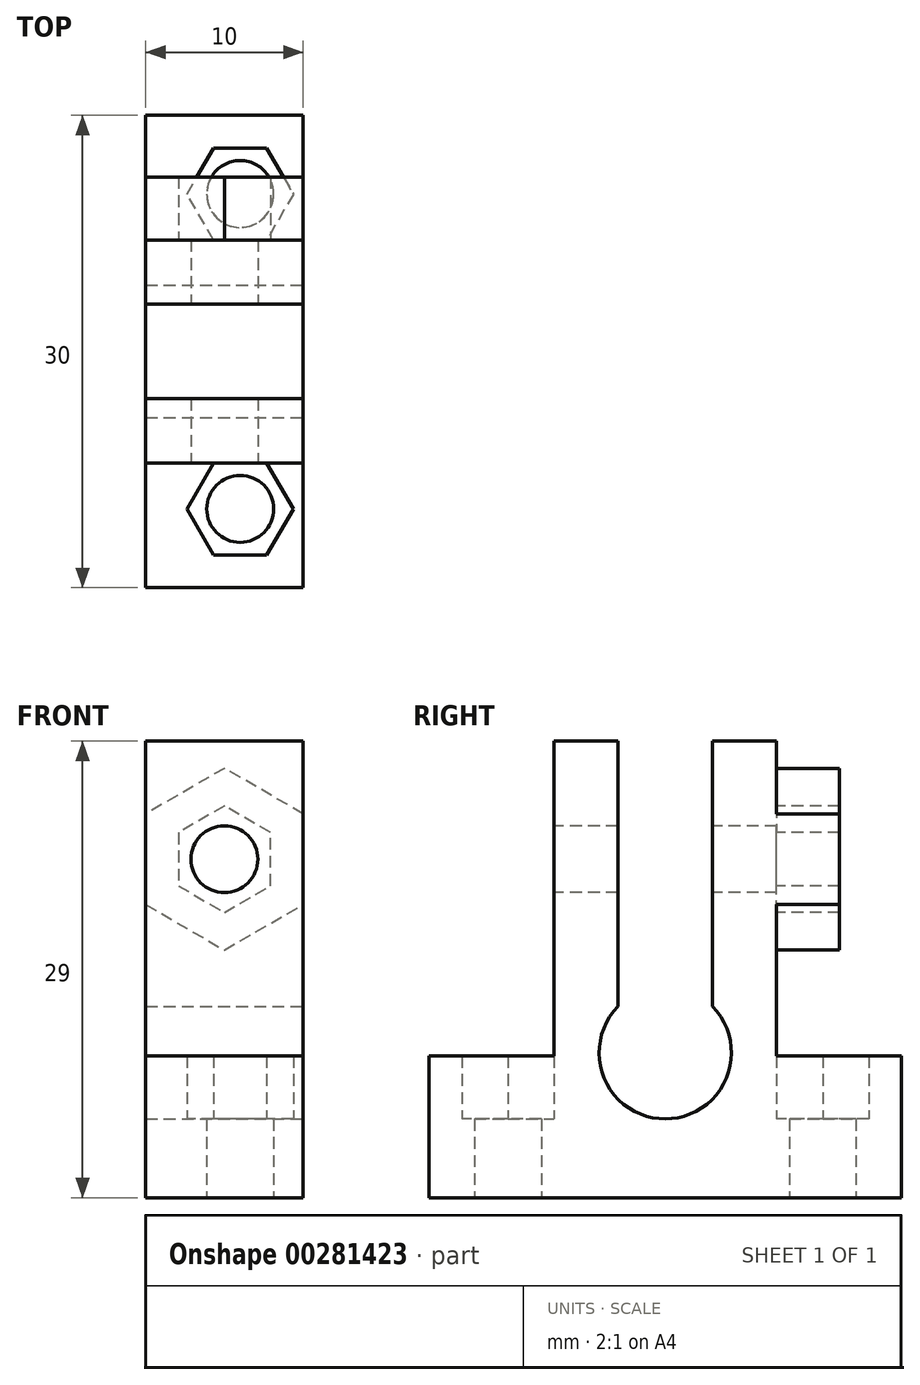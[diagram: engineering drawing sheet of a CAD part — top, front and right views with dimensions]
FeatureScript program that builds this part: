
annotation { "Feature Type Name" : "Feature", "Feature Type Description" : "" }
export const myFeature = defineFeature(function(context is Context, id is Id, definition is map)
    precondition{}
    {
        {
            var Q0;
            Q0=qCreatedBy(makeId("Top.planeOp"),FACE);
            var sketch = newSketch(context, id + "F0", { "sketchPlane" : qUnion([Q0])});
            skLineSegment(sketch, "E0.bottom", {"start": v(5, -15) * mm, "end": v(-5, -15) * mm});
            skLineSegment(sketch, "E0.top", {"start": v(5, 15) * mm, "end": v(-5, 15) * mm});
            skLineSegment(sketch, "E0.left", {"start": v(5, -15) * mm, "end": v(5, 15) * mm});
            skLineSegment(sketch, "E0.right", {"start": v(-5, -15) * mm, "end": v(-5, 15) * mm});
            skPoint(sketch, "E0.middle", {"position": v(0, 0) * mm});
            skCircle(sketch, "E1", {"center": v(1, 10) * mm, "radius": 2.12 * mm});
            skCircle(sketch, "E2", {"center": v(1, -10) * mm, "radius": 2.12 * mm});
            skSolve(sketch);
        }
        {
            var Q0;
            Q0=qSketchRegion(id+"F0",true);
            extrude(context, id + "F1", {"entities" : qUnion([Q0]), "depth" : 5 * mm});
        }
        {
            var Q0;
            Q0=makeQuery(id+"F1.opExtrude","CAP_FACE",FACE,{"disambiguationData":[OSD([sQuery(id+"F0.wireOp",EDGE,"E0.bottom"),sQuery(id+"F0.wireOp",EDGE,"E0.top"),sQuery(id+"F0.wireOp",EDGE,"E0.left"),sQuery(id+"F0.wireOp",EDGE,"E0.right"),sQuery(id+"F0.wireOp",EDGE,"E1"),sQuery(id+"F0.wireOp",EDGE,"E2")])],"isStart":false});
            var sketch = newSketch(context, id + "F2", { "sketchPlane" : qUnion([Q0])});
            skCircle(sketch, "E3.cCircle", {"center": v(1, 10) * mm, "radius": 2.93 * mm, "construction": true});
            skLineSegment(sketch, "E3.0", {"start": v(2.69, 7.07) * mm, "end": v(-0.69, 7.07) * mm});
            skLineSegment(sketch, "E3.1", {"start": v(-0.69, 7.07) * mm, "end": v(-2.38, 10) * mm});
            skLineSegment(sketch, "E3.2", {"start": v(-2.38, 10) * mm, "end": v(-0.69, 12.92) * mm});
            skLineSegment(sketch, "E3.3", {"start": v(-0.69, 12.92) * mm, "end": v(2.69, 12.92) * mm});
            skLineSegment(sketch, "E3.4", {"start": v(2.69, 12.92) * mm, "end": v(4.38, 10) * mm});
            skLineSegment(sketch, "E3.5", {"start": v(4.38, 10) * mm, "end": v(2.69, 7.07) * mm});
            skPoint(sketch, "E3.0.midPoint", {"position": v(1, 7.07) * mm});
            skLineSegment(sketch, "E4.MirrorCS", {"start": v(2.69, -7.07) * mm, "end": v(-0.69, -7.07) * mm});
            skLineSegment(sketch, "E5.MirrorCS", {"start": v(4.38, -10) * mm, "end": v(2.69, -7.07) * mm});
            skLineSegment(sketch, "E6.MirrorCS", {"start": v(2.69, -12.92) * mm, "end": v(4.38, -10) * mm});
            skLineSegment(sketch, "E7.MirrorCS", {"start": v(-0.69, -12.92) * mm, "end": v(2.69, -12.92) * mm});
            skLineSegment(sketch, "E8.MirrorCS", {"start": v(-2.38, -10) * mm, "end": v(-0.69, -12.92) * mm});
            skLineSegment(sketch, "E9.MirrorCS", {"start": v(-0.69, -7.07) * mm, "end": v(-2.38, -10) * mm});
            skCircle(sketch, "E10.MirrorC", {"center": v(1, -10) * mm, "radius": 2.93 * mm, "construction": true});
            skPoint(sketch, "E11.MirrorP", {"position": v(1, -7.07) * mm});
            skLineSegment(sketch, "E12.bottom", {"start": v(-5, 15) * mm, "end": v(5, 15) * mm});
            skLineSegment(sketch, "E12.top", {"start": v(-5, -15) * mm, "end": v(5, -15) * mm});
            skLineSegment(sketch, "E12.left", {"start": v(-5, 15) * mm, "end": v(-5, -15) * mm});
            skLineSegment(sketch, "E12.right", {"start": v(5, 15) * mm, "end": v(5, -15) * mm});
            skSolve(sketch);
        }
        {
            var Q0;
            Q0=qSketchRegion(id+"F2",true);
            extrude(context, id + "F3", {"entities" : qUnion([Q0]), "operationType" : NewBodyOperationType.ADD, "depth" : 4 * mm});
        }
        {
            var Q0;
            Q0=makeQuery(id+"F3.opExtrude","CAP_FACE",FACE,{"disambiguationData":[OSD([sQuery(id+"F2.wireOp",EDGE,"E3.0"),sQuery(id+"F2.wireOp",EDGE,"E3.1"),sQuery(id+"F2.wireOp",EDGE,"E3.2"),sQuery(id+"F2.wireOp",EDGE,"E3.3"),sQuery(id+"F2.wireOp",EDGE,"E3.4"),sQuery(id+"F2.wireOp",EDGE,"E3.5"),sQuery(id+"F2.wireOp",EDGE,"E4.MirrorCS"),sQuery(id+"F2.wireOp",EDGE,"E5.MirrorCS"),sQuery(id+"F2.wireOp",EDGE,"E6.MirrorCS"),sQuery(id+"F2.wireOp",EDGE,"E7.MirrorCS"),sQuery(id+"F2.wireOp",EDGE,"E8.MirrorCS"),sQuery(id+"F2.wireOp",EDGE,"E9.MirrorCS"),sQuery(id+"F2.wireOp",EDGE,"E12.bottom"),sQuery(id+"F2.wireOp",EDGE,"E12.top"),sQuery(id+"F2.wireOp",EDGE,"E12.left"),sQuery(id+"F2.wireOp",EDGE,"E12.right")])],"isStart":false});
            var sketch = newSketch(context, id + "F4", { "sketchPlane" : qUnion([Q0])});
            skLineSegment(sketch, "E13.bottom", {"start": v(-5, 7.07) * mm, "end": v(5, 7.07) * mm});
            skLineSegment(sketch, "E13.top", {"start": v(-5, -7.07) * mm, "end": v(5, -7.07) * mm});
            skLineSegment(sketch, "E13.left", {"start": v(-5, 7.07) * mm, "end": v(-5, -7.07) * mm});
            skLineSegment(sketch, "E13.right", {"start": v(5, 7.07) * mm, "end": v(5, -7.07) * mm});
            skSolve(sketch);
        }
        {
            var Q0;
            Q0=qSketchRegion(id+"F4",true);
            extrude(context, id + "F5", {"entities" : qUnion([Q0]), "operationType" : NewBodyOperationType.ADD, "depth" : 20 * mm});
        }
        {
            var Q0;
            Q0=makeQuery(id+"F5.boolean.opBoolean","MERGE",FACE,{"derivedFrom":[makeQuery(id+"F3.boolean.opBoolean","MERGE",FACE,{"derivedFrom":[makeQuery(id+"F1.opExtrude","SWEPT_FACE",FACE,{"disambiguationData":[OSD([sQuery(id+"F0.wireOp",EDGE,"E0.left")])]}),makeQuery(id+"F3.opExtrude","SWEPT_FACE",FACE,{"disambiguationData":[OSD([sQuery(id+"F2.wireOp",EDGE,"E12.right")])]})]}),makeQuery(id+"F5.opExtrude","SWEPT_FACE",FACE,{"disambiguationData":[OSD([sQuery(id+"F4.wireOp",EDGE,"E13.right")])]})]});
            var sketch = newSketch(context, id + "F6", { "sketchPlane" : qUnion([Q0])});
            skArc(sketch, "E14", {"start": v(3, 12.14) * mm, "mid": v(0, 5) * mm, "end": v(-3, 12.14) * mm});
            skLineSegment(sketch, "E15", {"start": v(-3, 29) * mm, "end": v(-3, 12.14) * mm});
            skLineSegment(sketch, "E16", {"start": v(-3, 29) * mm, "end": v(3, 29) * mm});
            skLineSegment(sketch, "E17", {"start": v(3, 29) * mm, "end": v(3, 12.14) * mm});
            skLineSegment(sketch, "E18", {"start": v(0, 5) * mm, "end": v(0, 0) * mm, "construction": true});
            skSolve(sketch);
        }
        {
            var Q0;
            Q0=qSketchRegion(id+"F6",true);
            extrude(context, id + "F7", {"entities" : qUnion([Q0]), "operationType" : NewBodyOperationType.REMOVE, "endBound" : BoundingType.THROUGH_ALL, "oppositeDirection" : true, "depth" : 25 * mm});
        }
        {
            var Q0;
            Q0=makeQuery(id+"F5.boolean.opBoolean","MERGE",FACE,{"derivedFrom":[makeQuery(id+"F3.opExtrude","SWEPT_FACE",FACE,{"disambiguationData":[OSD([sQuery(id+"F2.wireOp",EDGE,"E4.MirrorCS")])]}),makeQuery(id+"F5.opExtrude","SWEPT_FACE",FACE,{"disambiguationData":[OSD([sQuery(id+"F4.wireOp",EDGE,"E13.top")])]})]});
            var sketch = newSketch(context, id + "F8", { "sketchPlane" : qUnion([Q0])});
            skCircle(sketch, "E19", {"center": v(0, 21.5) * mm, "radius": 2.12 * mm});
            skSolve(sketch);
        }
        {
            var Q0;
            Q0=qSketchRegion(id+"F8",true);
            extrude(context, id + "F9", {"entities" : qUnion([Q0]), "operationType" : NewBodyOperationType.REMOVE, "endBound" : BoundingType.THROUGH_ALL, "oppositeDirection" : true, "depth" : 25 * mm});
        }
        {
            var Q0;
            Q0=makeQuery(id+"F5.boolean.opBoolean","MERGE",FACE,{"derivedFrom":[makeQuery(id+"F3.opExtrude","SWEPT_FACE",FACE,{"disambiguationData":[OSD([sQuery(id+"F2.wireOp",EDGE,"E3.0")])]}),makeQuery(id+"F5.opExtrude","SWEPT_FACE",FACE,{"disambiguationData":[OSD([sQuery(id+"F4.wireOp",EDGE,"E13.bottom")])]})]});
            var sketch = newSketch(context, id + "F10", { "sketchPlane" : qUnion([Q0])});
            skCircle(sketch, "E20.cCircle", {"center": v(0, 21.5) * mm, "radius": 5 * mm, "construction": true});
            skLineSegment(sketch, "E20.0", {"start": v(5, 24.39) * mm, "end": v(5, 18.61) * mm});
            skLineSegment(sketch, "E20.1", {"start": v(5, 18.61) * mm, "end": v(0, 15.73) * mm});
            skLineSegment(sketch, "E20.2", {"start": v(0, 15.73) * mm, "end": v(-5, 18.61) * mm});
            skLineSegment(sketch, "E20.3", {"start": v(-5, 18.61) * mm, "end": v(-5, 24.39) * mm});
            skLineSegment(sketch, "E20.4", {"start": v(-5, 24.39) * mm, "end": v(0, 27.27) * mm});
            skLineSegment(sketch, "E20.5", {"start": v(0, 27.27) * mm, "end": v(5, 24.39) * mm});
            skPoint(sketch, "E20.0.midPoint", {"position": v(5, 21.5) * mm});
            skCircle(sketch, "E21.cCircle", {"center": v(0, 21.5) * mm, "radius": 2.93 * mm, "construction": true});
            skLineSegment(sketch, "E21.0", {"start": v(2.93, 23.19) * mm, "end": v(2.93, 19.81) * mm});
            skLineSegment(sketch, "E21.1", {"start": v(2.93, 19.81) * mm, "end": v(0, 18.12) * mm});
            skLineSegment(sketch, "E21.2", {"start": v(0, 18.12) * mm, "end": v(-2.93, 19.81) * mm});
            skLineSegment(sketch, "E21.3", {"start": v(-2.93, 19.81) * mm, "end": v(-2.93, 23.19) * mm});
            skLineSegment(sketch, "E21.4", {"start": v(-2.92, 23.19) * mm, "end": v(0, 24.88) * mm});
            skLineSegment(sketch, "E21.5", {"start": v(0, 24.88) * mm, "end": v(2.93, 23.19) * mm});
            skPoint(sketch, "E21.0.midPoint", {"position": v(2.93, 21.5) * mm});
            skSolve(sketch);
        }
        {
            var Q0;
            Q0=qSketchRegion(id+"F10",true);
            extrude(context, id + "F11", {"entities" : qUnion([Q0]), "operationType" : NewBodyOperationType.ADD, "depth" : 4 * mm});
        }
    });
